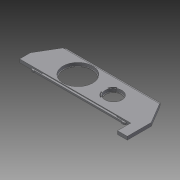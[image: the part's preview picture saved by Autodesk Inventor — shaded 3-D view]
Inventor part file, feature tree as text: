
AUTODESK INVENTOR PART (.ipt)
format: ipt  version: 2013 (Build 170138000, 138)  size: 259,072 bytes
history: native  units: mm
features: extrude x10, sketch x9, projected_geometry x3
ambient origin geometry x8: Origin, YZ Plane, XZ Plane, XY Plane, X Axis, Y Axis, Z Axis, Center Point
bodies: Solid1 (feature_tree)
feature tree (22):
  extrude  "Extrusion1"  Depth=143.0mm
  extrude  "Extrusion2"  Depth=50.0mm
  extrude  "Extrusion3"  Depth=20.0mm
  extrude  "Extrusion4"  Depth=2.75mm
  extrude  "Extrusion5"  Depth=2.75mm
  sketch  "Sketch6"  dims[d18=1.2mm d19=0.0mm d20=2.6mm]
  extrude  "Extrusion6"  Depth=2.6mm
  extrude  "Extrusion7"  Depth=3.8mm TaperAngle=0.0deg
  extrude  "Extrusion13"  Depth=132.75mm
  extrude  "Extrusion14"  Depth=1.25mm
  extrude  "Extrusion16"  TaperAngle=0.0deg  [1 undecoded]
  sketch  "Sketch1"  dims[d2=16.2mm d4=143.0mm]
  sketch  "Sketch2"  dims[d5=183.0mm d6=50.0mm]
  sketch  "Sketch3"  dims[d7=14.8mm d8=20.0mm]
  sketch  "Sketch4"  dims[d9=5.0mm d10=0.0mm d11=2.75mm]
  sketch  "Sketch5"  dims[d12=1.2mm d13=0.0mm d17=2.75mm]
  projected_geometry  "Projected Loop1"
  sketch  "Sketch11"  dims[d22=143.0mm d23=3.8mm d24=0.0mm]
  sketch  "Sketch12"  dims[d25=1.0mm d27=132.75mm]
  sketch  "Sketch13"  dims[d28=15.0mm d29=1.25mm d30=0.0mm d31=0.0mm d32=45.0mm d35=25.5mm d37=64.5mm d38=64.5mm d39=1.0mm d40=1.0mm d41=0.0mm d42=0.0mm d43=4.5mm d44=0.0mm d87=27.0mm d88=1.0mm d89=1.0mm d90=120.0deg d93=120.0deg d94=6.981317mm d95=6.981317mm d98=0.0mm d99=0.0mm d100=0.698132mm d101=0.698132mm d102=0.0mm d103=0.0mm d104=1.047198mm d105=1.047198mm d106=0.523599mm d107=0.523599mm d113=0.5mm d114=0.0mm]
  projected_geometry  "Projected Loop2"
  projected_geometry  "Projected Loop3"
note: 1 required parameter value undecoded (feature->parameter linkage not recoverable at this tier; creation-order binding heuristic only, values carry confidence <= 0.55)
